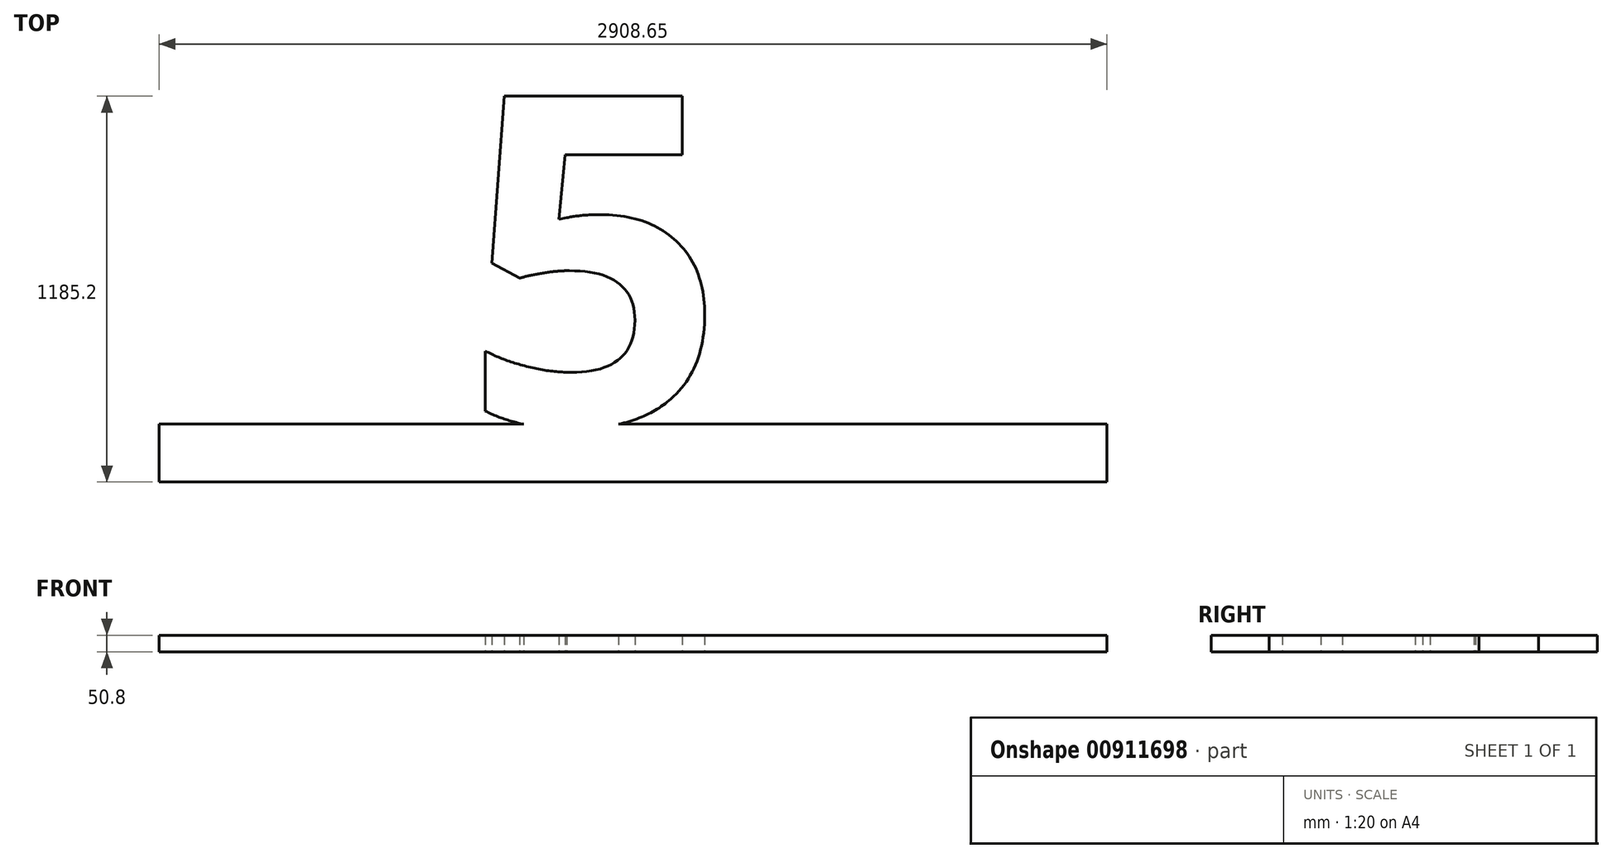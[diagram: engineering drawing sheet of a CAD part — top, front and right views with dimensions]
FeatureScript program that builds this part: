
annotation { "Feature Type Name" : "Feature", "Feature Type Description" : "" }
export const myFeature = defineFeature(function(context is Context, id is Id, definition is map)
    precondition{}
    {
        {
            var Q0;
            Q0=qCreatedBy(makeId("Top.planeOp"),FACE);
            var sketch = newSketch(context, id + "F0", { "sketchPlane" : qUnion([Q0])});
            skLineSegment(sketch, "E0.bottom", {"start": v(-283.71, -177.8) * mm, "end": v(2624.94, -177.8) * mm});
            skLineSegment(sketch, "E0.top", {"start": v(-283.71, 0) * mm, "end": v(2624.94, 0) * mm});
            skLineSegment(sketch, "E0.left", {"start": v(-283.71, -177.8) * mm, "end": v(-283.71, 0) * mm});
            skLineSegment(sketch, "E0.right", {"start": v(2624.94, -177.8) * mm, "end": v(2624.94, 0) * mm});
            skText(sketch, "E1", { "text": "15H", "fontName": "OpenSans-Bold.ttf"});
            const initialGuessF0  = {"E1": [-0.15671, 0, 1, 0, 1.016]};
            skSetInitialGuess(sketch, initialGuessF0);
            skSolve(sketch);
        }
        {
            var Q0;
            {var subQ0=sQuery(id+"F0.wireOp",EDGE,"d5d90416-0cdc-48ac-b64b-d5d0caaf983f.sketch_text.stroke-12");var subQ1=sQuery(id+"F0.wireOp",EDGE,"E0.top");var subQ2=makeQuery(id+"F0.imprint","INTERSECT",VERTEX,{"derivedFrom":[subQ1,subQ0]});Q0=makeQuery(id+"F0.imprint","IMPRINT",FACE,{"disambiguationData":[TD([[makeQuery(id+"F0.imprint","IMPRINT",EDGE,{"disambiguationData":[TD([[subQ2,-1.0]])],"derivedFrom":subQ1}),-1.0]])]});}
            var Q1;
            {var subQ6=sQuery(id+"F0.wireOp",EDGE,"d5d90416-0cdc-48ac-b64b-d5d0caaf983f.sketch_text.stroke-10");Q1=makeQuery(id+"F0.imprint","IMPRINT",FACE,{"disambiguationData":[TD([[makeQuery(id+"F0.imprint","IMPRINT",EDGE,{"derivedFrom":subQ6}),-1.0]])]});}
            var Q2;
            Q2=makeQuery(id+"F0.imprint","IMPRINT",FACE,{"disambiguationData":[TD([[makeQuery(id+"F0.imprint","IMPRINT",EDGE,{"derivedFrom":sQuery(id+"F0.wireOp",EDGE,"E0.bottom")}),1.0]])]});
            var Q3;
            Q3=makeQuery(id+"F0.imprint","IMPRINT",FACE,{"disambiguationData":[TD([[makeQuery(id+"F0.imprint","IMPRINT",EDGE,{"derivedFrom":sQuery(id+"F0.wireOp",EDGE,"d5d90416-0cdc-48ac-b64b-d5d0caaf983f.sketch_text.stroke-26")}),-1.0]])]});
            var Q4;
            Q4=makeQuery(id+"F0.imprint","IMPRINT",FACE,{"disambiguationData":[TD([[makeQuery(id+"F0.imprint","IMPRINT",EDGE,{"derivedFrom":sQuery(id+"F0.wireOp",EDGE,"d5d90416-0cdc-48ac-b64b-d5d0caaf983f.sketch_text.stroke-0")}),-1.0]])]});
            var Q5;
            Q5=makeQuery(id+"F0.imprint","IMPRINT",FACE,{"disambiguationData":[TD([[makeQuery(id+"F0.imprint","IMPRINT",EDGE,{"derivedFrom":sQuery(id+"F0.wireOp",EDGE,"eadfe806-04ac-4918-bb0a-3f37c2bbbc6a.sketch_text.stroke-10")}),-1.0]])]});
            var Q6;
            Q6=makeQuery(id+"F0.imprint","IMPRINT",FACE,{"disambiguationData":[TD([[makeQuery(id+"F0.imprint","IMPRINT",EDGE,{"derivedFrom":sQuery(id+"F0.wireOp",EDGE,"eadfe806-04ac-4918-bb0a-3f37c2bbbc6a.sketch_text.stroke-0")}),-1.0]])]});
            var Q7;
            Q7=makeQuery(id+"F0.imprint","IMPRINT",FACE,{"disambiguationData":[TD([[makeQuery(id+"F0.imprint","IMPRINT",EDGE,{"derivedFrom":sQuery(id+"F0.wireOp",EDGE,"eadfe806-04ac-4918-bb0a-3f37c2bbbc6a.sketch_text.stroke-20")}),-1.0]])]});
            var Q8;
            Q8=makeQuery(id+"F0.imprint","IMPRINT",FACE,{"disambiguationData":[TD([[makeQuery(id+"F0.imprint","IMPRINT",EDGE,{"derivedFrom":sQuery(id+"F0.wireOp",EDGE,"7b9dad4d-f56e-4f66-a96d-e45d99efa82c.sketch_text.stroke-0")}),-1.0]])]});
            var Q9;
            Q9=makeQuery(id+"F0.imprint","IMPRINT",FACE,{"disambiguationData":[TD([[makeQuery(id+"F0.imprint","IMPRINT",EDGE,{"derivedFrom":sQuery(id+"F0.wireOp",EDGE,"7b9dad4d-f56e-4f66-a96d-e45d99efa82c.sketch_text.stroke-10")}),-1.0]])]});
            var Q10;
            Q10=makeQuery(id+"F0.imprint","IMPRINT",FACE,{"disambiguationData":[TD([[makeQuery(id+"F0.imprint","IMPRINT",EDGE,{"derivedFrom":sQuery(id+"F0.wireOp",EDGE,"7b9dad4d-f56e-4f66-a96d-e45d99efa82c.sketch_text.stroke-34")}),-1.0]])]});
            var Q11;
            {var subQ0=sQuery(id+"F0.wireOp",EDGE,"dcbf4fd3-fc6b-438e-9322-ba9460cc3787.sketch_text.stroke-17");var subQ1=sQuery(id+"F0.wireOp",EDGE,"E0.top");var subQ2=makeQuery(id+"F0.imprint","INTERSECT",VERTEX,{"derivedFrom":[subQ1,subQ0]});Q11=makeQuery(id+"F0.imprint","IMPRINT",FACE,{"disambiguationData":[TD([[makeQuery(id+"F0.imprint","IMPRINT",EDGE,{"disambiguationData":[TD([[subQ2,-1.0]])],"derivedFrom":subQ1}),-1.0]])]});}
            var Q12;
            Q12=makeQuery(id+"F0.imprint","IMPRINT",FACE,{"disambiguationData":[TD([[makeQuery(id+"F0.imprint","IMPRINT",EDGE,{"derivedFrom":sQuery(id+"F0.wireOp",EDGE,"dcbf4fd3-fc6b-438e-9322-ba9460cc3787.sketch_text.stroke-10")}),-1.0]])]});
            var Q13;
            Q13=makeQuery(id+"F0.imprint","IMPRINT",FACE,{"disambiguationData":[TD([[makeQuery(id+"F0.imprint","IMPRINT",EDGE,{"derivedFrom":sQuery(id+"F0.wireOp",EDGE,"dcbf4fd3-fc6b-438e-9322-ba9460cc3787.sketch_text.stroke-37")}),-1.0]])]});
            var Q14;
            Q14=makeQuery(id+"F0.imprint","IMPRINT",FACE,{"disambiguationData":[TD([[makeQuery(id+"F0.imprint","IMPRINT",EDGE,{"derivedFrom":sQuery(id+"F0.wireOp",EDGE,"dcbf4fd3-fc6b-438e-9322-ba9460cc3787.sketch_text.stroke-0")}),-1.0]])]});
            var Q15;
            Q15=makeQuery(id+"F0.imprint","IMPRINT",FACE,{"disambiguationData":[TD([[makeQuery(id+"F0.imprint","IMPRINT",EDGE,{"derivedFrom":sQuery(id+"F0.wireOp",EDGE,"9d91f46f-ca5a-4a3c-b455-d203b070acd4.sketch_text.stroke-10")}),-1.0]])]});
            var Q16;
            Q16=makeQuery(id+"F0.imprint","IMPRINT",FACE,{"disambiguationData":[TD([[makeQuery(id+"F0.imprint","IMPRINT",EDGE,{"derivedFrom":sQuery(id+"F0.wireOp",EDGE,"9d91f46f-ca5a-4a3c-b455-d203b070acd4.sketch_text.stroke-28")}),-1.0]])]});
            var Q17;
            Q17=makeQuery(id+"F0.imprint","IMPRINT",FACE,{"disambiguationData":[TD([[makeQuery(id+"F0.imprint","IMPRINT",EDGE,{"derivedFrom":sQuery(id+"F0.wireOp",EDGE,"9d91f46f-ca5a-4a3c-b455-d203b070acd4.sketch_text.stroke-0")}),-1.0]])]});
            var Q18;
            Q18=makeQuery(id+"F0.imprint","IMPRINT",FACE,{"disambiguationData":[TD([[makeQuery(id+"F0.imprint","IMPRINT",EDGE,{"derivedFrom":sQuery(id+"F0.wireOp",EDGE,"E1.sketch_text.stroke-10")}),-1.0]])]});
            var Q19;
            Q19=makeQuery(id+"F0.imprint","IMPRINT",FACE,{"disambiguationData":[TD([[makeQuery(id+"F0.imprint","IMPRINT",EDGE,{"derivedFrom":sQuery(id+"F0.wireOp",EDGE,"E1.sketch_text.stroke-30")}),-1.0]])]});
            var Q20;
            Q20=makeQuery(id+"F0.imprint","IMPRINT",FACE,{"disambiguationData":[TD([[makeQuery(id+"F0.imprint","IMPRINT",EDGE,{"derivedFrom":sQuery(id+"F0.wireOp",EDGE,"E1.sketch_text.stroke-0")}),-1.0]])]});
            var Q21;
            {var subQ0=sQuery(id+"F0.wireOp",EDGE,"E1.sketch_text.stroke-14");var subQ1=sQuery(id+"F0.wireOp",EDGE,"E0.top");var subQ2=makeQuery(id+"F0.imprint","INTERSECT",VERTEX,{"derivedFrom":[subQ1,subQ0]});Q21=makeQuery(id+"F0.imprint","IMPRINT",FACE,{"disambiguationData":[TD([[makeQuery(id+"F0.imprint","IMPRINT",EDGE,{"disambiguationData":[TD([[subQ2,-1.0]])],"derivedFrom":subQ1}),-1.0]])]});}
            extrude(context, id + "F1", {"entities" : qUnion([Q0, Q1, Q2, Q3, Q4, Q5, Q6, Q7, Q8, Q9, Q10, Q11, Q12, Q13, Q14, Q15, Q16, Q17, Q18, Q19, Q20, Q21]), "depth" : 50.8 * mm, "offsetDistance" : 25.4 * mm});
        }
    });
